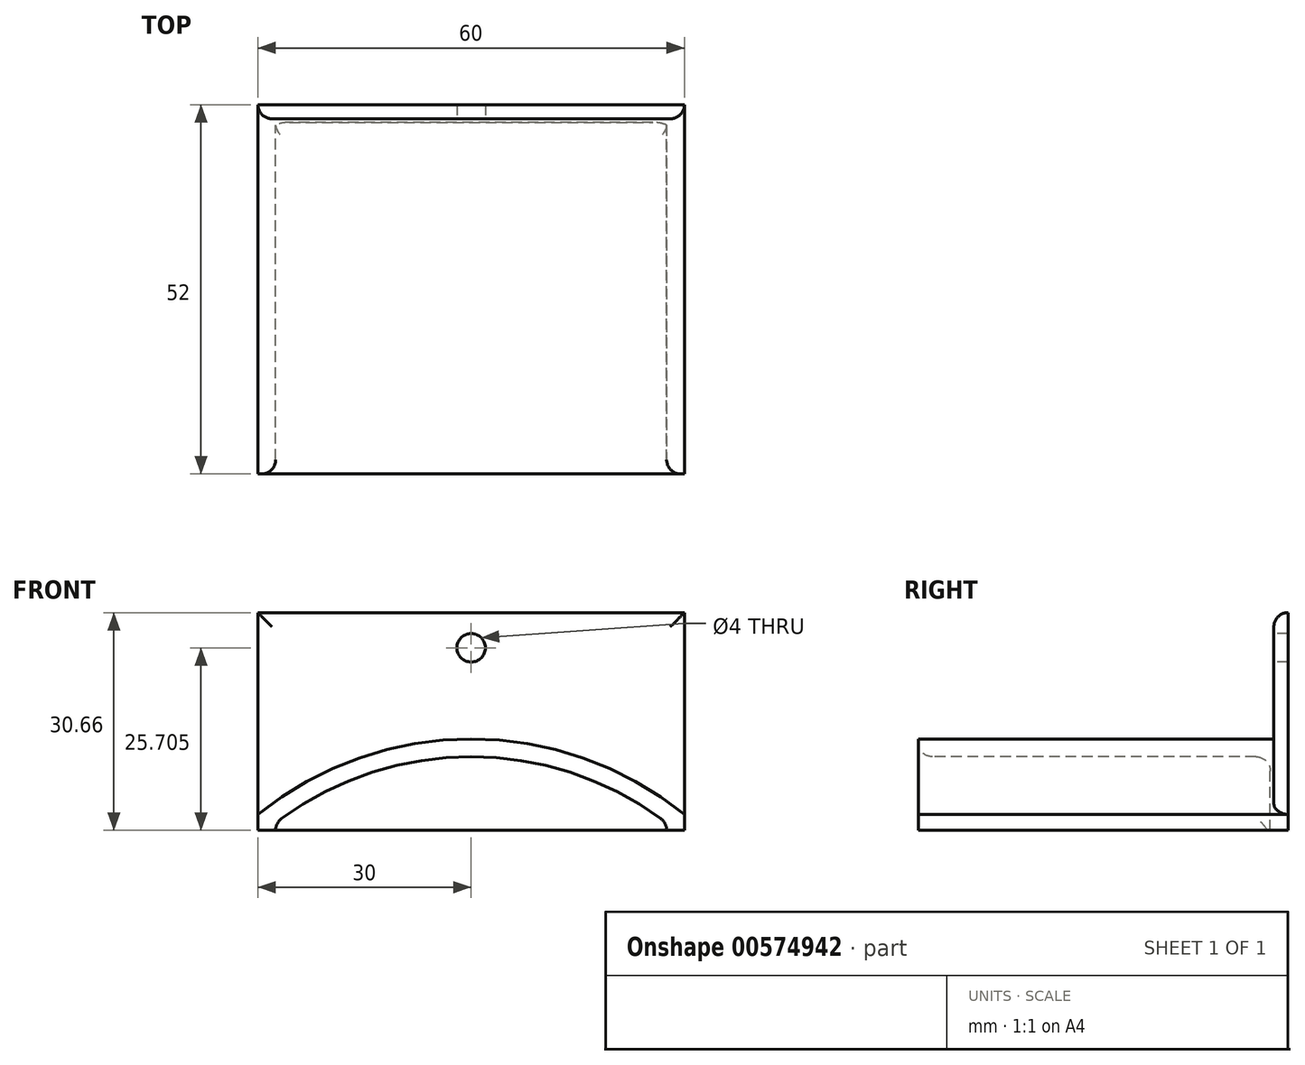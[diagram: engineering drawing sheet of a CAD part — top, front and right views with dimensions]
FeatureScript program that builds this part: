
annotation { "Feature Type Name" : "Feature", "Feature Type Description" : "" }
export const myFeature = defineFeature(function(context is Context, id is Id, definition is map)
    precondition{}
    {
        {
            var Q0;
            Q0=qCreatedBy(makeId("Top.planeOp"),FACE);
            var sketch = newSketch(context, id + "F0", { "sketchPlane" : qUnion([Q0])});
            skLineSegment(sketch, "E0.bottom", {"start": v(30, -25) * mm, "end": v(-30, -25) * mm});
            skLineSegment(sketch, "E0.top", {"start": v(30, 25) * mm, "end": v(-30, 25) * mm});
            skLineSegment(sketch, "E0.left", {"start": v(30, -25) * mm, "end": v(30, 25) * mm});
            skLineSegment(sketch, "E0.right", {"start": v(-30, -25) * mm, "end": v(-30, 25) * mm});
            skPoint(sketch, "E0.middle", {"position": v(0, 0) * mm});
            skSolve(sketch);
        }
        {
            var Q0;
            Q0=makeQuery(id+"F0.imprint","IMPRINT",FACE,{"disambiguationData":[TD([[makeQuery(id+"F0.imprint","IMPRINT",EDGE,{"derivedFrom":sQuery(id+"F0.wireOp",EDGE,"E0.bottom")}),-1.0]])]});
            extrude(context, id + "F1", {"entities" : qUnion([Q0]), "depth" : 25 * mm, "offsetDistance" : 25 * mm});
        }
        {
            var Q0;
            Q0=makeQuery(id+"F1.opExtrude","SWEPT_FACE",FACE,{"disambiguationData":[OSD([sQuery(id+"F0.wireOp",EDGE,"E0.bottom")])]});
            var sketch = newSketch(context, id + "F2", { "sketchPlane" : qUnion([Q0])});
            skLineSegment(sketch, "E1", {"start": v(30, 2.25) * mm, "end": v(-30, 2.25) * mm, "construction": true});
            skArc(sketch, "E2", {"start": v(30, 2.25) * mm, "mid": v(0, 12.87) * mm, "end": v(-30, 2.25) * mm});
            skSolve(sketch);
        }
        {
            var Q0;
            {var subQ0=sQuery(id+"F2.wireOp",EDGE,"E2");Q0=makeQuery(id+"F2.imprint","IMPRINT",FACE,{"disambiguationData":[TD([[makeQuery(id+"F2.imprint","IMPRINT",EDGE,{"derivedFrom":subQ0}),-1.0]])]});}
            extrude(context, id + "F3", {"entities" : qUnion([Q0]), "operationType" : NewBodyOperationType.REMOVE, "endBound" : BoundingType.THROUGH_ALL, "oppositeDirection" : true, "depth" : 25 * mm, "offsetDistance" : 25 * mm});
        }
        {
            var Q0;
            Q0=makeQuery(id+"F1.opExtrude","SWEPT_FACE",FACE,{"disambiguationData":[OSD([sQuery(id+"F0.wireOp",EDGE,"E0.top")])]});
            var sketch = newSketch(context, id + "F4", { "sketchPlane" : qUnion([Q0])});
            skPoint(sketch, "E3.0", {"position": v(-30, 0) * mm});
            skPoint(sketch, "E3.1", {"position": v(30, 0) * mm});
            skLineSegment(sketch, "E4.bottom", {"start": v(-30, 0) * mm, "end": v(30, 0) * mm});
            skLineSegment(sketch, "E4.top", {"start": v(-30, 30.66) * mm, "end": v(30, 30.66) * mm});
            skLineSegment(sketch, "E4.left", {"start": v(-30, 0) * mm, "end": v(-30, 30.66) * mm});
            skLineSegment(sketch, "E4.right", {"start": v(30, 0) * mm, "end": v(30, 30.66) * mm});
            skSolve(sketch);
        }
        {
            var Q0;
            Q0 = qSketchRegion(id + "F4", true);
            extrude(context, id + "F5", {"entities" : qUnion([Q0]), "operationType" : NewBodyOperationType.ADD, "depth" : 2 * mm, "offsetDistance" : 25 * mm});
        }
        {
            var Q0;
            Q0=makeQuery(id+"F5.opExtrude","CAP_FACE",FACE,{"disambiguationData":[OSD([sQuery(id+"F4.wireOp",EDGE,"E4.bottom"),sQuery(id+"F4.wireOp",EDGE,"E4.top"),sQuery(id+"F4.wireOp",EDGE,"E4.left"),sQuery(id+"F4.wireOp",EDGE,"E4.right")])],"isStart":true});
            var sketch = newSketch(context, id + "F6", { "sketchPlane" : qUnion([Q0])});
            skCircle(sketch, "E5", {"center": v(0, 25.7) * mm, "radius": 2 * mm});
            skSolve(sketch);
        }
        {
            var Q0;
            Q0=makeQuery(id+"F6.imprint","IMPRINT",FACE,{"disambiguationData":[TD([[makeQuery(id+"F6.imprint","IMPRINT",EDGE,{"derivedFrom":sQuery(id+"F6.wireOp",EDGE,"E5")}),1.0]])]});
            extrude(context, id + "F7", {"entities" : qUnion([Q0]), "operationType" : NewBodyOperationType.REMOVE, "endBound" : BoundingType.THROUGH_ALL, "oppositeDirection" : true, "depth" : 25 * mm, "offsetDistance" : 25 * mm});
        }
        {
            var Q0;
            Q0=makeQuery(id+"F5.boolean.opBoolean","MERGE",FACE,{"derivedFrom":[makeQuery(id+"F1.opExtrude","CAP_FACE",FACE,{"disambiguationData":[OSD([sQuery(id+"F0.wireOp",EDGE,"E0.bottom"),sQuery(id+"F0.wireOp",EDGE,"E0.top"),sQuery(id+"F0.wireOp",EDGE,"E0.left"),sQuery(id+"F0.wireOp",EDGE,"E0.right")])],"isStart":true}),makeQuery(id+"F5.opExtrude","SWEPT_FACE",FACE,{"disambiguationData":[OSD([sQuery(id+"F4.wireOp",EDGE,"E4.bottom")])]})]});
            shell(context, id + "F8", {"entities" : qUnion([Q0]), "thickness" : 2.5 * mm});
        }
        {
            var Q0;
            Q0=makeQuery(id+"F8.opShell","OFFSET_FACE",FACE,{"disambiguationData":[OSD([sQuery(id+"F0.wireOp",EDGE,"E0.bottom")])]});
            extrude(context, id + "F9", {"entities" : qUnion([Q0]), "operationType" : NewBodyOperationType.REMOVE, "oppositeDirection" : true, "depth" : 25 * mm, "offsetDistance" : 25 * mm});
        }
        {
            var Q0;
            Q0=makeQuery(id+"F8.opShell","TWEAK_EDGE",EDGE,{"derivedFrom":[makeQuery(id+"F3.boolean.opBoolean","COPY",FACE,{"derivedFrom":makeQuery(id+"F3.opExtrude","SWEPT_FACE",FACE,{"disambiguationData":[OSD([sQuery(id+"F2.wireOp",EDGE,"E2")])]})}),makeQuery(id+"F5.opExtrude","CAP_FACE",FACE,{"disambiguationData":[OSD([sQuery(id+"F4.wireOp",EDGE,"E4.bottom"),sQuery(id+"F4.wireOp",EDGE,"E4.top"),sQuery(id+"F4.wireOp",EDGE,"E4.left"),sQuery(id+"F4.wireOp",EDGE,"E4.right")])],"isStart":false})]});
            var Q1;
            {var subQ0=sQuery(id+"F2.wireOp",EDGE,"E2");var subQ1=sQuery(id+"F0.wireOp",EDGE,"E0.right");var subQ2=sQuery(id+"F0.wireOp",EDGE,"E0.bottom");Q1=makeQuery(id+"F9.boolean.opBoolean","MERGE",EDGE,{"derivedFrom":[makeQuery(id+"F8.opShell","OFFSET_EDGE",EDGE,{"disambiguationData":[OSD([subQ2,subQ1,subQ0])]}),makeQuery(id+"F9.opExtrude","SWEPT_EDGE",EDGE,{"disambiguationData":[OSD([subQ2,subQ1,subQ0])]})]});}
            var Q2;
            {var subQ0=sQuery(id+"F2.wireOp",EDGE,"E2");var subQ1=sQuery(id+"F0.wireOp",EDGE,"E0.left");var subQ2=sQuery(id+"F0.wireOp",EDGE,"E0.bottom");Q2=makeQuery(id+"F9.boolean.opBoolean","MERGE",EDGE,{"derivedFrom":[makeQuery(id+"F8.opShell","OFFSET_EDGE",EDGE,{"disambiguationData":[OSD([subQ2,subQ1,subQ0])]}),makeQuery(id+"F9.opExtrude","SWEPT_EDGE",EDGE,{"disambiguationData":[OSD([subQ2,subQ1,subQ0])]})]});}
            var Q3;
            Q3=makeQuery(id+"F3.boolean.opBoolean","COPY",EDGE,{"derivedFrom":makeQuery(id+"F3.opExtrude","SWEPT_EDGE",EDGE,{"disambiguationData":[OSD([sQuery(id+"F0.wireOp",EDGE,"E0.bottom"),sQuery(id+"F0.wireOp",EDGE,"E0.right"),sQuery(id+"F2.wireOp",EDGE,"E2")])]})});
            var Q4;
            Q4=makeQuery(id+"F3.boolean.opBoolean","COPY",EDGE,{"derivedFrom":makeQuery(id+"F3.opExtrude","SWEPT_EDGE",EDGE,{"disambiguationData":[OSD([sQuery(id+"F0.wireOp",EDGE,"E0.bottom"),sQuery(id+"F0.wireOp",EDGE,"E0.left"),sQuery(id+"F2.wireOp",EDGE,"E2")])]})});
            var Q5;
            Q5=makeQuery(id+"F5.opExtrude","CAP_EDGE",EDGE,{"disambiguationData":[OSD([sQuery(id+"F4.wireOp",EDGE,"E4.top")])],"isStart":true});
            var Q6;
            Q6=makeQuery(id+"F5.opExtrude","CAP_EDGE",EDGE,{"disambiguationData":[OSD([sQuery(id+"F4.wireOp",EDGE,"E4.right")])],"isStart":true});
            var Q7;
            Q7=makeQuery(id+"F5.opExtrude","CAP_EDGE",EDGE,{"disambiguationData":[OSD([sQuery(id+"F4.wireOp",EDGE,"E4.left")])],"isStart":true});
            var Q8;
            Q8=makeQuery(id+"F3.boolean.opBoolean","COPY",EDGE,{"derivedFrom":makeQuery(id+"F3.opExtrude","CAP_EDGE",EDGE,{"disambiguationData":[OSD([sQuery(id+"F2.wireOp",EDGE,"E2")])],"isStart":true})});
            var Q9;
            Q9=makeQuery(id+"F9.boolean.opBoolean","INTERSECT",EDGE,{"derivedFrom":[makeQuery(id+"F1.opExtrude","SWEPT_FACE",FACE,{"disambiguationData":[OSD([sQuery(id+"F0.wireOp",EDGE,"E0.bottom")])]}),makeQuery(id+"F9.opExtrude","SWEPT_FACE",FACE,{"disambiguationData":[OSD([sQuery(id+"F2.wireOp",EDGE,"E2")])]})]});
            fillet(context, id + "F10", {"entities" : qUnion([Q0, Q1, Q2, Q3, Q4, Q5, Q6, Q7, Q8, Q9]), "radius" : 2 * mm, "tangentPropagation" : true, "allowEdgeOverflow" : false});
        }
    });
